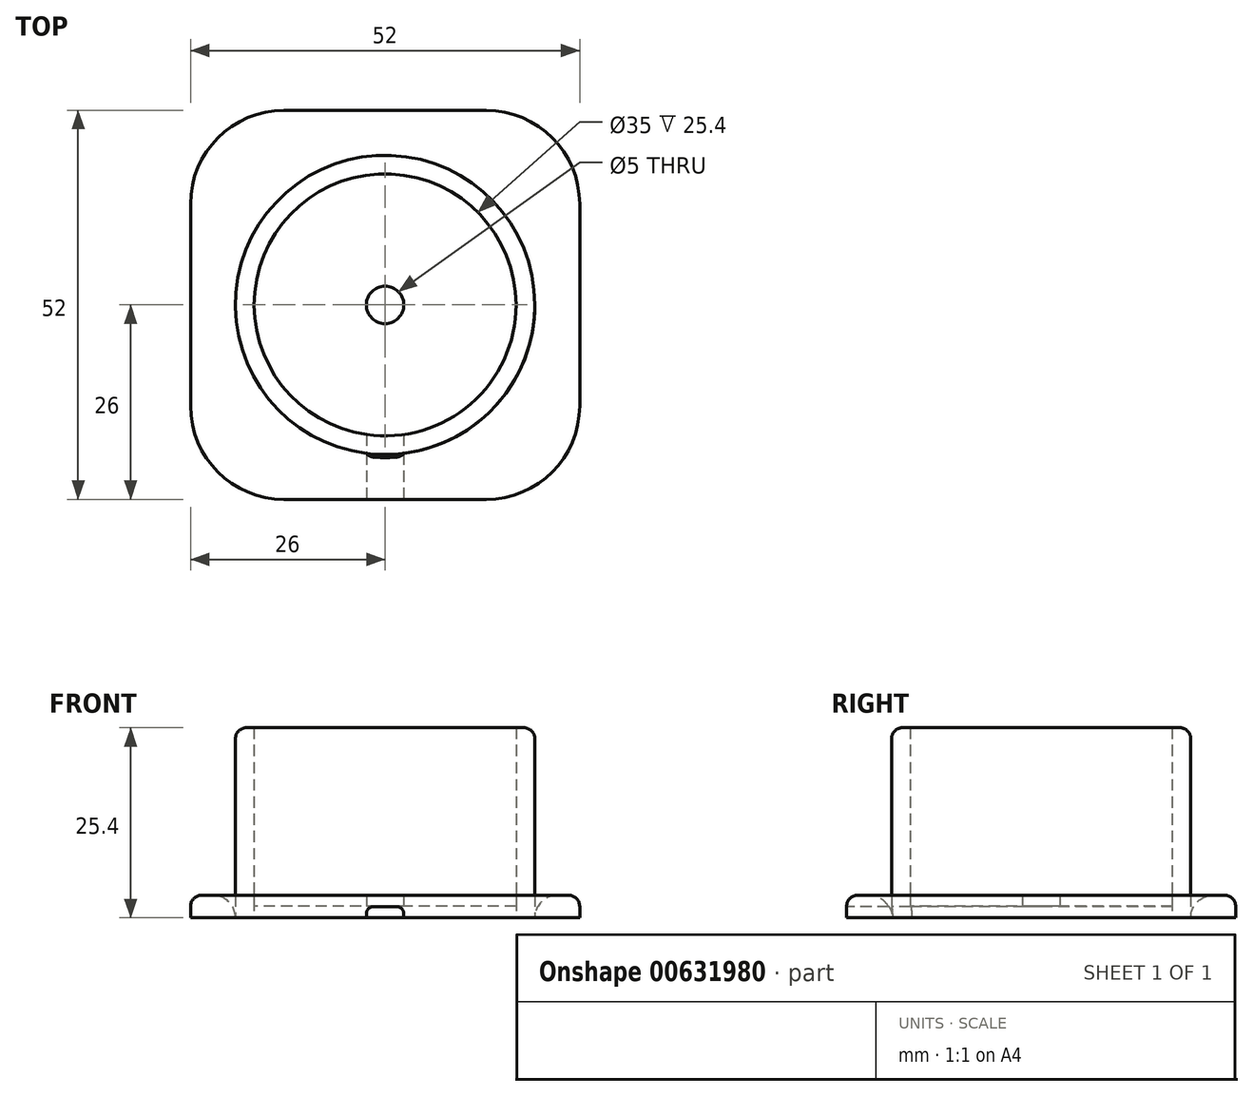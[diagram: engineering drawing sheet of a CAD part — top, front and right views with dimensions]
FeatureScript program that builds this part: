
annotation { "Feature Type Name" : "Feature", "Feature Type Description" : "" }
export const myFeature = defineFeature(function(context is Context, id is Id, definition is map)
    precondition{}
    {
        {
            var Q0;
            Q0=qCreatedBy(makeId("Top.planeOp"),FACE);
            var sketch = newSketch(context, id + "F0", { "sketchPlane" : qUnion([Q0])});
            skCircle(sketch, "E0", {"center": v(0, 0) * mm, "radius": 17.5 * mm});
            skCircle(sketch, "E1", {"center": v(0, 0) * mm, "radius": 20 * mm});
            skLineSegment(sketch, "E2.bottom", {"start": v(26, 26) * mm, "end": v(-26, 26) * mm});
            skLineSegment(sketch, "E2.top", {"start": v(26, -26) * mm, "end": v(-26, -26) * mm});
            skLineSegment(sketch, "E2.left", {"start": v(26, 26) * mm, "end": v(26, -26) * mm});
            skLineSegment(sketch, "E2.right", {"start": v(-26, 26) * mm, "end": v(-26, -26) * mm});
            skCircle(sketch, "E3", {"center": v(0, 0) * mm, "radius": 2.5 * mm});
            skSolve(sketch);
        }
        {
            var Q0;
            Q0 = qSketchRegion(id + "F0", true);
            var Q1;
            Q1=makeQuery(id+"F0.imprint","IMPRINT",FACE,{"disambiguationData":[TD([[makeQuery(id+"F0.imprint","IMPRINT",EDGE,{"derivedFrom":sQuery(id+"F0.wireOp",EDGE,"E0")}),1.0]])]});
            extrude(context, id + "F1", {"entities" : qUnion([Q0, Q1]), "depth" : 3 * mm, "offsetDistance" : 25 * mm});
        }
        {
            var Q0;
            Q0=makeQuery(id+"F0.imprint","IMPRINT",FACE,{"disambiguationData":[TD([[makeQuery(id+"F0.imprint","IMPRINT",EDGE,{"derivedFrom":sQuery(id+"F0.wireOp",EDGE,"E0")}),-1.0]])]});
            extrude(context, id + "F2", {"entities" : qUnion([Q0]), "depth" : 25.4 * mm, "offsetDistance" : 25 * mm});
        }
        {
            var Q0;
            Q0=makeQuery(id+"F0.imprint","IMPRINT",FACE,{"disambiguationData":[TD([[makeQuery(id+"F0.imprint","IMPRINT",EDGE,{"derivedFrom":sQuery(id+"F0.wireOp",EDGE,"E0")}),1.0]])]});
            extrude(context, id + "F3", {"entities" : qUnion([Q0]), "operationType" : NewBodyOperationType.REMOVE, "depth" : 1.55 * mm, "offsetDistance" : 25 * mm});
        }
        {
            var Q0;
            Q0=makeQuery(id+"F1.opExtrude","SWEPT_EDGE",EDGE,{"disambiguationData":[OSD([sQuery(id+"F0.wireOp",EDGE,"E2.bottom"),sQuery(id+"F0.wireOp",EDGE,"E2.right")])]});
            var Q1;
            Q1=makeQuery(id+"F1.opExtrude","SWEPT_EDGE",EDGE,{"disambiguationData":[OSD([sQuery(id+"F0.wireOp",EDGE,"E2.bottom"),sQuery(id+"F0.wireOp",EDGE,"E2.left")])]});
            var Q2;
            Q2=makeQuery(id+"F1.opExtrude","SWEPT_EDGE",EDGE,{"disambiguationData":[OSD([sQuery(id+"F0.wireOp",EDGE,"E2.top"),sQuery(id+"F0.wireOp",EDGE,"E2.left")])]});
            var Q3;
            Q3=makeQuery(id+"F1.opExtrude","SWEPT_EDGE",EDGE,{"disambiguationData":[OSD([sQuery(id+"F0.wireOp",EDGE,"E2.top"),sQuery(id+"F0.wireOp",EDGE,"E2.right")])]});
            fillet(context, id + "F4", {"entities" : qUnion([Q0, Q1, Q2, Q3]), "radius" : 12.5 * mm, "tangentPropagation" : true, "allowEdgeOverflow" : false});
        }
        {
            var Q0;
            Q0=makeQuery(id+"F2.opExtrude","CAP_EDGE",EDGE,{"disambiguationData":[OSD([sQuery(id+"F0.wireOp",EDGE,"E1")])],"isStart":false});
            var Q1;
            Q1=makeQuery(id+"F1.opExtrude","CAP_EDGE",EDGE,{"disambiguationData":[OSD([sQuery(id+"F0.wireOp",EDGE,"E2.top")])],"isStart":false});
            fillet(context, id + "F5", {"entities" : qUnion([Q0, Q1]), "radius" : 1.5 * mm, "tangentPropagation" : true, "allowEdgeOverflow" : false});
        }
        {
            var Q0;
            Q0=makeQuery(id+"F1.opExtrude","CAP_EDGE",EDGE,{"disambiguationData":[OSD([sQuery(id+"F0.wireOp",EDGE,"E1")])],"isStart":false});
            fillet(context, id + "F6", {"entities" : qUnion([Q0]), "radius" : 3 * mm, "tangentPropagation" : true, "allowEdgeOverflow" : false});
        }
        {
            var Q0;
            Q0=makeQuery(id+"F1.opExtrude","SWEPT_FACE",FACE,{"disambiguationData":[OSD([sQuery(id+"F0.wireOp",EDGE,"E2.top")])]});
            var sketch = newSketch(context, id + "F7", { "sketchPlane" : qUnion([Q0])});
            skLineSegment(sketch, "E4.bottom", {"start": v(-2.5, 1.5) * mm, "end": v(2.5, 1.5) * mm, "construction": true});
            skLineSegment(sketch, "E4.top", {"start": v(-2.5, -1.5) * mm, "end": v(2.5, -1.5) * mm, "construction": true});
            skLineSegment(sketch, "E4.left", {"start": v(-2.5, 1.5) * mm, "end": v(-2.5, -1.5) * mm, "construction": true});
            skLineSegment(sketch, "E4.right", {"start": v(2.5, 1.5) * mm, "end": v(2.5, -1.5) * mm, "construction": true});
            skPoint(sketch, "E4.middle", {"position": v(0, 0) * mm});
            skLineSegment(sketch, "E5.bottom", {"start": v(-2.5, 0) * mm, "end": v(2.5, 0) * mm});
            skLineSegment(sketch, "E5.top", {"start": v(-2.5, 1.5) * mm, "end": v(2.5, 1.5) * mm});
            skLineSegment(sketch, "E5.left", {"start": v(-2.5, 0) * mm, "end": v(-2.5, 1.5) * mm});
            skLineSegment(sketch, "E5.right", {"start": v(2.5, 0) * mm, "end": v(2.5, 1.5) * mm});
            skSolve(sketch);
        }
        {
            var Q0;
            Q0 = qSketchRegion(id + "F7", true);
            extrude(context, id + "F8", {"entities" : qUnion([Q0]), "operationType" : NewBodyOperationType.REMOVE, "oppositeDirection" : true, "depth" : 25.4 * mm, "offsetDistance" : 25 * mm});
        }
        {
            var Q0;
            Q0=makeQuery(id+"F8.boolean.opBoolean","COPY",EDGE,{"derivedFrom":makeQuery(id+"F8.opExtrude","SWEPT_EDGE",EDGE,{"disambiguationData":[OSD([sQuery(id+"F0.wireOp",EDGE,"E2.top"),sQuery(id+"F7.wireOp",EDGE,"E5.top"),sQuery(id+"F7.wireOp",EDGE,"E5.left")])]})});
            var Q1;
            Q1=makeQuery(id+"F8.boolean.opBoolean","COPY",EDGE,{"derivedFrom":makeQuery(id+"F8.opExtrude","SWEPT_EDGE",EDGE,{"disambiguationData":[OSD([sQuery(id+"F0.wireOp",EDGE,"E2.top"),sQuery(id+"F7.wireOp",EDGE,"E5.top"),sQuery(id+"F7.wireOp",EDGE,"E5.right")])]})});
            fillet(context, id + "F9", {"entities" : qUnion([Q0, Q1]), "radius" : 1 * mm, "tangentPropagation" : true, "allowEdgeOverflow" : false});
        }
    });
